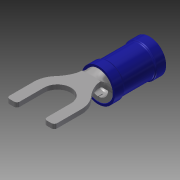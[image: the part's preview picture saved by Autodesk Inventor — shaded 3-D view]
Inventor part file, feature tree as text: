
AUTODESK INVENTOR PART (.ipt)
format: ipt  version: 2014 (Build 180170000, 170)  size: 446,976 bytes
history: native  units: in
note: dims shown in document units (in); Inventor stores cm internally (conversion verified against a paired STEP export)
features: fillet x6, sketch x6, projected_geometry x5, extrude x4, mirror x1, shell x1, revolve x1, plane x1, loft x1, chamfer x1, other x1
ambient origin geometry x8: Origin, YZ Plane, XZ Plane, XY Plane, X Axis, Y Axis, Z Axis, Center Point
bodies: Solid1 (feature_tree), Solid2 (feature_tree)
feature tree (28):
  extrude  "Extrusion1"  Depth=0.229in TaperAngle=0.0deg
  extrude  "Extrusion2"  Depth=0.01in TaperAngle=0.0deg
  fillet  "Fillet1"  Radius=0.01in
  mirror  "Mirror1"
  shell  "Shell1"  Thickness=0.0175in
  revolve  "Revolution1"  [1 undecoded]
  plane  "Work Plane1"
  extrude  "Extrusion3"  Depth=0.082in
  loft  "Loft1"
  fillet  "Fillet2"  Radius=0.073in
  fillet  "Fillet3"  Radius=0.032in
  fillet  "Fillet4"  [1 undecoded]
  fillet  "Fillet5"  [1 undecoded]
  chamfer  "Chamfer1"  Distance=0.015in
  extrude  "Extrusion4"  Depth=0.02in
  fillet  "Fillet6"  Radius=0.02in
  sketch  "Sketch1"  dims[d0=0.219in d1=0.229in d2=0.0in]
  sketch  "Sketch2"  dims[d3=0.236in d4=0.068in d5=0.0in d6=0.01in d7=0.0175in]
  projected_geometry  "Projected Loop1"
  sketch  "Sketch3"  dims[d8=0.031in d9=0.031in]
  sketch  "Sketch4"  dims[d10=90.0deg d11=0.082in]
  projected_geometry  "Projected Loop2"
  sketch  "Sketch5"  dims[d12=0.2905in d13=0.0495in d14=0.339in d15=0.073in d16=0.032in d17=0.0in d18=0.0in d19=90.0deg d20=0.0in d21=90.0deg]
  projected_geometry  "Projected Loop3"
  other  "Edges1"
  sketch  "Sketch6"  dims[d22=0.1in d23=0.015in d24=0.02in d25=0.02in d26=0.003in d27=0.125in d28=45.0deg d29=0.005in d30=0.032in d31=0.0in d32=0.289in d33=0.02in]
  projected_geometry  "Project Cut Edges1"
  projected_geometry  "Project Cut Edges2"
note: 3 required parameter values undecoded (feature->parameter linkage not recoverable at this tier; creation-order binding heuristic only, values carry confidence <= 0.55)